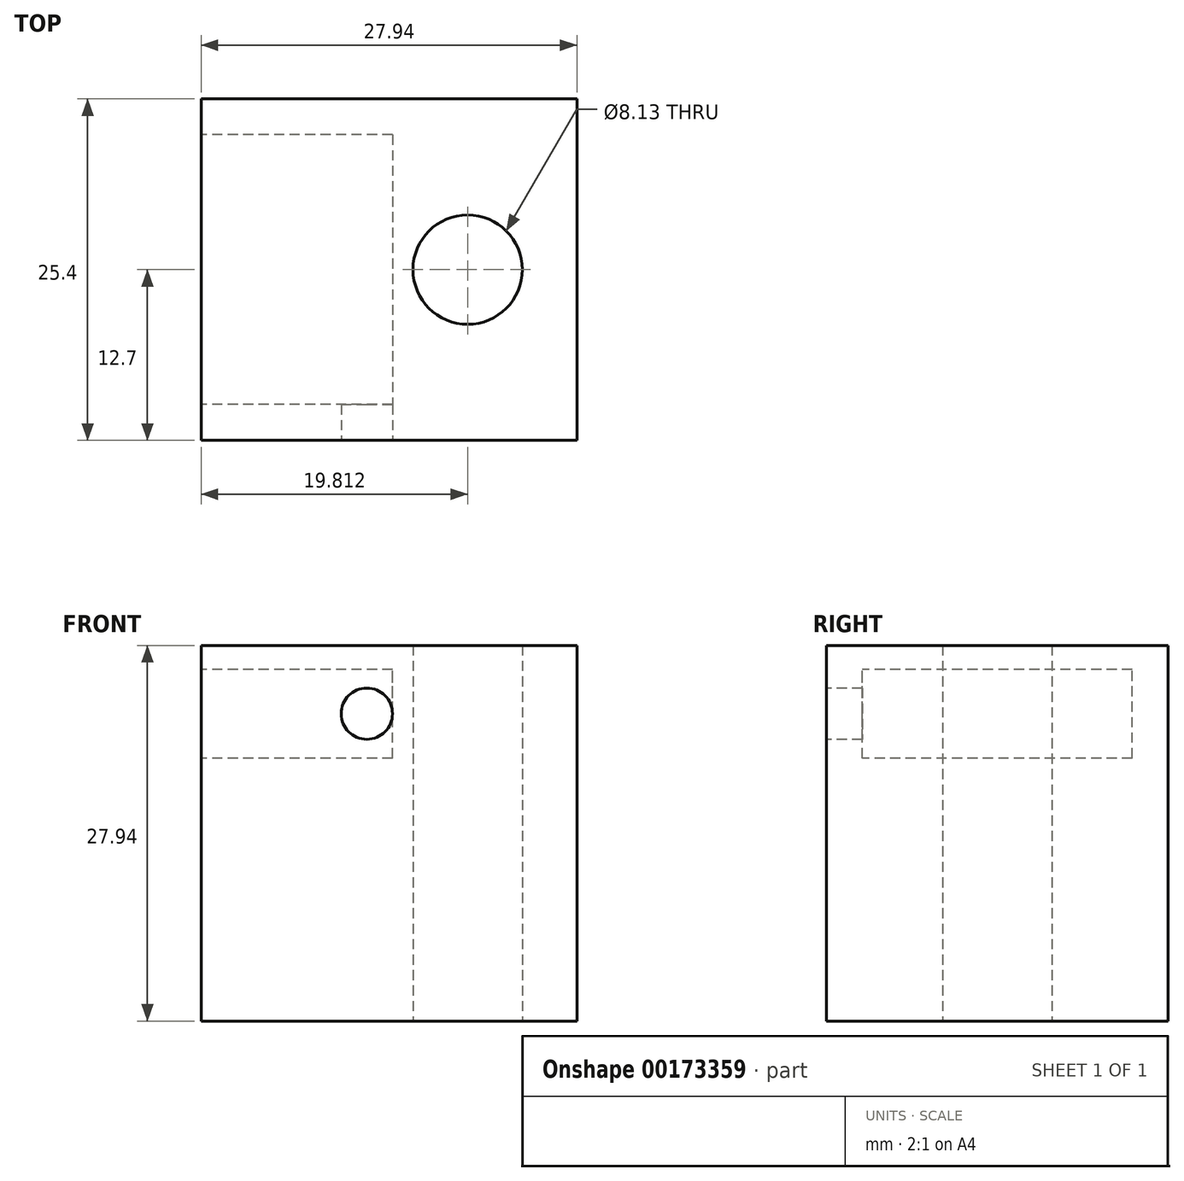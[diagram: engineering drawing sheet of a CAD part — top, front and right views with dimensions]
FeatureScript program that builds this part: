
annotation { "Feature Type Name" : "Feature", "Feature Type Description" : "" }
export const myFeature = defineFeature(function(context is Context, id is Id, definition is map)
    precondition{}
    {
        {
            var Q0;
            Q0=qCreatedBy(makeId("Top.planeOp"),FACE);
            var sketch = newSketch(context, id + "F0", { "sketchPlane" : qUnion([Q0])});
            skLineSegment(sketch, "E0.bottom", {"start": v(-25.4, 12.7) * mm, "end": v(2.54, 12.7) * mm});
            skLineSegment(sketch, "E0.top", {"start": v(-25.4, -12.7) * mm, "end": v(2.54, -12.7) * mm});
            skLineSegment(sketch, "E0.left", {"start": v(-25.4, 12.7) * mm, "end": v(-25.4, -12.7) * mm});
            skLineSegment(sketch, "E0.right", {"start": v(2.54, 12.7) * mm, "end": v(2.54, -12.7) * mm});
            skCircle(sketch, "E1", {"center": v(-5.59, 0) * mm, "radius": 4.06 * mm});
            skSolve(sketch);
        }
        {
            var Q0;
            Q0=makeQuery(id+"F0.imprint","IMPRINT",FACE,{"disambiguationData":[TD([[makeQuery(id+"F0.imprint","IMPRINT",EDGE,{"derivedFrom":sQuery(id+"F0.wireOp",EDGE,"E0.bottom")}),-1.0]])]});
            extrude(context, id + "F1", {"entities" : qUnion([Q0]), "depth" : 10.16 * mm});
        }
        {
            var Q0;
            Q0=makeQuery(id+"F1.opExtrude","SWEPT_FACE",FACE,{"disambiguationData":[OSD([sQuery(id+"F0.wireOp",EDGE,"E0.left")])]});
            var sketch = newSketch(context, id + "F2", { "sketchPlane" : qUnion([Q0])});
            skLineSegment(sketch, "E2.bottom", {"start": v(-10.03, 1.78) * mm, "end": v(10.03, 1.78) * mm});
            skLineSegment(sketch, "E2.top", {"start": v(-10.03, 8.38) * mm, "end": v(10.03, 8.38) * mm});
            skLineSegment(sketch, "E2.left", {"start": v(-10.03, 1.78) * mm, "end": v(-10.03, 8.38) * mm});
            skLineSegment(sketch, "E2.right", {"start": v(10.03, 1.78) * mm, "end": v(10.03, 8.38) * mm});
            skSolve(sketch);
        }
        {
            var Q0;
            Q0 = qSketchRegion(id + "F2", true);
            extrude(context, id + "F3", {"entities" : qUnion([Q0]), "operationType" : NewBodyOperationType.REMOVE, "oppositeDirection" : true, "depth" : 14.22 * mm});
        }
        {
            var Q0;
            Q0=makeQuery(id+"F1.opExtrude","SWEPT_FACE",FACE,{"disambiguationData":[OSD([sQuery(id+"F0.wireOp",EDGE,"E0.top")])]});
            var sketch = newSketch(context, id + "F4", { "sketchPlane" : qUnion([Q0])});
            skCircle(sketch, "E3", {"center": v(-13.08, 5.08) * mm, "radius": 1.9 * mm});
            skSolve(sketch);
        }
        {
            var Q0;
            Q0 = qSketchRegion(id + "F4", true);
            extrude(context, id + "F5", {"entities" : qUnion([Q0]), "operationType" : NewBodyOperationType.REMOVE, "oppositeDirection" : true, "depth" : 3.02 * mm});
        }
        {
            var Q0;
            Q0=makeQuery(id+"F0.imprint","IMPRINT",FACE,{"disambiguationData":[TD([[makeQuery(id+"F0.imprint","IMPRINT",EDGE,{"derivedFrom":sQuery(id+"F0.wireOp",EDGE,"E0.bottom")}),-1.0]])]});
            extrude(context, id + "F6", {"entities" : qUnion([Q0]), "operationType" : NewBodyOperationType.ADD, "oppositeDirection" : true, "depth" : 17.78 * mm});
        }
    });
